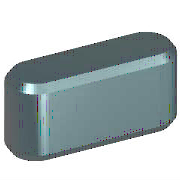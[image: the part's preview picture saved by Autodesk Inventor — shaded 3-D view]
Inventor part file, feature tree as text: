
AUTODESK INVENTOR PART (.ipt)
format: ipt  version: 2025 (Build 290162000, 162)  size: 139,264 bytes
history: native  units: mm (DEFAULTED — no unit token found)
features: plane x3, extrude x1
ambient origin geometry x8: Origin, YZ Plane, XZ Plane, XY Plane, X Axis, Y Axis, Z Axis, Center Point
bodies: Solid1 (feature_tree)
feature tree (4):
  plane  "Work Plane1"
  plane  "Work Plane2"
  extrude  "轴承体1"  Depth=6.0mm
  plane  "Work Plane3"
